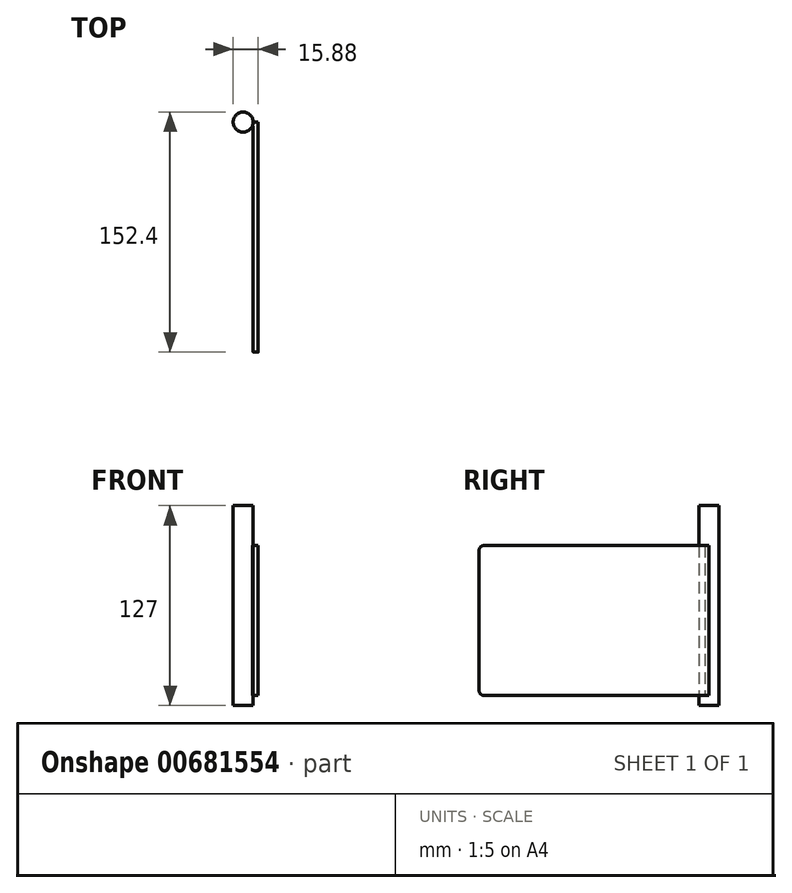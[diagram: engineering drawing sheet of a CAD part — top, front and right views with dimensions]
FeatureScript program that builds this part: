
annotation { "Feature Type Name" : "Feature", "Feature Type Description" : "" }
export const myFeature = defineFeature(function(context is Context, id is Id, definition is map)
    precondition{}
    {
        {
            var Q0;
            Q0=qCreatedBy(makeId("Top.planeOp"),FACE);
            var sketch = newSketch(context, id + "F0", { "sketchPlane" : qUnion([Q0])});
            skArc(sketch, "E0", {"start": v(6.35, 0) * mm, "mid": v(-6.22, 1.26) * mm, "end": v(5.85, -2.47) * mm});
            skLineSegment(sketch, "E1.bottom", {"start": v(6.35, 0) * mm, "end": v(9.53, 0) * mm});
            skLineSegment(sketch, "E1.top", {"start": v(6.35, -146.05) * mm, "end": v(9.53, -146.05) * mm});
            skLineSegment(sketch, "E1.left", {"start": v(6.35, -2.47) * mm, "end": v(6.35, -146.05) * mm});
            skLineSegment(sketch, "E1.right", {"start": v(9.53, 0) * mm, "end": v(9.53, -146.05) * mm});
            skLineSegment(sketch, "E2", {"start": v(5.85, -2.47) * mm, "end": v(6.35, -2.47) * mm});
            skSolve(sketch);
        }
        {
            var Q0;
            Q0 = qSketchRegion(id + "F0", true);
            extrude(context, id + "F1", {"entities" : qUnion([Q0]), "depth" : 95.25 * mm, "offsetDistance" : 25.4 * mm});
        }
        {
            var Q0;
            Q0=makeQuery(id+"F1.opExtrude","CAP_FACE",FACE,{"disambiguationData":[OSD([sQuery(id+"F0.wireOp",EDGE,"E0"),sQuery(id+"F0.wireOp",EDGE,"E1.bottom"),sQuery(id+"F0.wireOp",EDGE,"E1.top"),sQuery(id+"F0.wireOp",EDGE,"E1.left"),sQuery(id+"F0.wireOp",EDGE,"E1.right"),sQuery(id+"F0.wireOp",EDGE,"E2")])],"isStart":false});
            var sketch = newSketch(context, id + "F2", { "sketchPlane" : qUnion([Q0])});
            skCircle(sketch, "E3", {"center": v(0, 0) * mm, "radius": 6.35 * mm});
            skSolve(sketch);
        }
        {
            var Q0;
            Q0 = qSketchRegion(id + "F2", true);
            extrude(context, id + "F3", {"entities" : qUnion([Q0]), "operationType" : NewBodyOperationType.ADD, "depth" : 25.4 * mm, "offsetDistance" : 25.4 * mm});
        }
        {
            var Q0;
            Q0=makeQuery(id+"F1.opExtrude","CAP_FACE",FACE,{"disambiguationData":[OSD([sQuery(id+"F0.wireOp",EDGE,"E0"),sQuery(id+"F0.wireOp",EDGE,"E1.bottom"),sQuery(id+"F0.wireOp",EDGE,"E1.top"),sQuery(id+"F0.wireOp",EDGE,"E1.left"),sQuery(id+"F0.wireOp",EDGE,"E1.right"),sQuery(id+"F0.wireOp",EDGE,"E2")])],"isStart":true});
            var sketch = newSketch(context, id + "F4", { "sketchPlane" : qUnion([Q0])});
            skCircle(sketch, "E4", {"center": v(0, 0) * mm, "radius": 6.35 * mm});
            skSolve(sketch);
        }
        {
            var Q0;
            Q0 = qSketchRegion(id + "F4", true);
            extrude(context, id + "F5", {"entities" : qUnion([Q0]), "operationType" : NewBodyOperationType.ADD, "depth" : 6.35 * mm, "offsetDistance" : 25.4 * mm});
        }
        {
            var Q0;
            Q0=makeQuery(id+"F1.opExtrude","SWEPT_FACE",FACE,{"disambiguationData":[OSD([sQuery(id+"F0.wireOp",EDGE,"E1.right")])]});
            var sketch = newSketch(context, id + "F6", { "sketchPlane" : qUnion([Q0])});
            skPoint(sketch, "E5.visualSharp", {"position": v(-146.05, 95.25) * mm});
            skArc(sketch, "E5.filletArc", {"start": v(-142.88, 95.25) * mm, "mid": v(-145.12, 94.32) * mm, "end": v(-146.05, 92.08) * mm});
            skPoint(sketch, "E6.visualSharp", {"position": v(-146.05, 0) * mm});
            skArc(sketch, "E6.filletArc", {"start": v(-146.05, 3.18) * mm, "mid": v(-145.12, 0.93) * mm, "end": v(-142.88, 0) * mm});
            skLineSegment(sketch, "E7", {"start": v(-146.05, 92.08) * mm, "end": v(-146.05, 95.25) * mm});
            skLineSegment(sketch, "E8", {"start": v(-146.05, 3.18) * mm, "end": v(-146.05, 0) * mm});
            skLineSegment(sketch, "E9", {"start": v(-146.05, 0) * mm, "end": v(-142.88, 0) * mm});
            skLineSegment(sketch, "E10", {"start": v(-146.05, 95.25) * mm, "end": v(-142.88, 95.25) * mm});
            skSolve(sketch);
        }
        {
            var Q0;
            Q0 = qSketchRegion(id + "F6", true);
            extrude(context, id + "F7", {"entities" : qUnion([Q0]), "operationType" : NewBodyOperationType.REMOVE, "oppositeDirection" : true, "depth" : 25.4 * mm, "offsetDistance" : 25.4 * mm});
        }
    });
